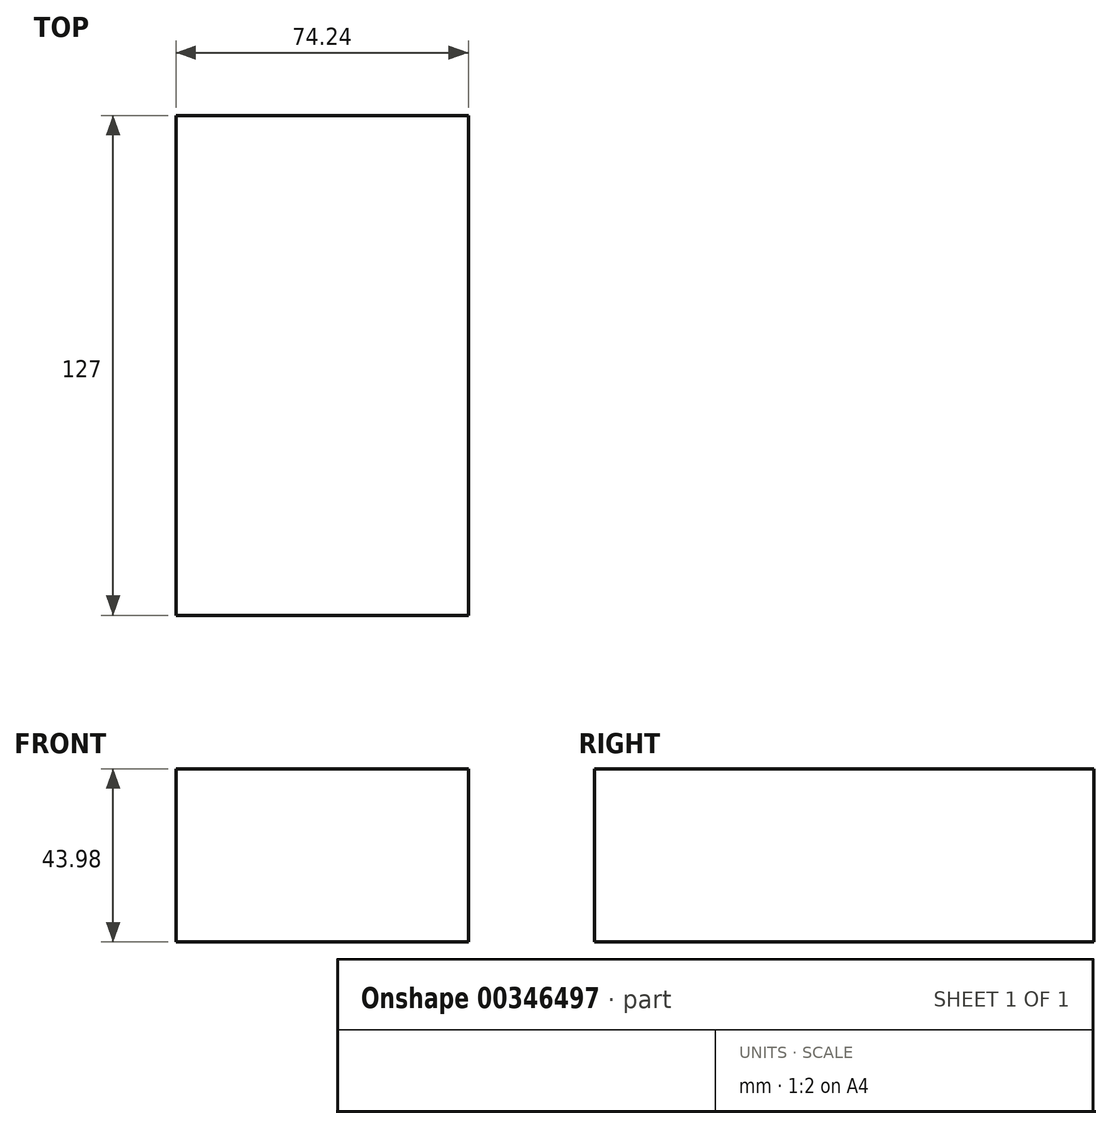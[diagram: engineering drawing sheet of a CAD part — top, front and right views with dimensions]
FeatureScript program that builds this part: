
annotation { "Feature Type Name" : "Feature", "Feature Type Description" : "" }
export const myFeature = defineFeature(function(context is Context, id is Id, definition is map)
    precondition{}
    {
        {
            var Q0;
            Q0=qCreatedBy(makeId("Front.planeOp"),FACE);
            var sketch = newSketch(context, id + "F0", { "sketchPlane" : qUnion([Q0])});
            skLineSegment(sketch, "E0.bottom", {"start": v(-37.12, -22) * mm, "end": v(37.12, -22) * mm});
            skLineSegment(sketch, "E0.top", {"start": v(-37.12, 22) * mm, "end": v(37.12, 22) * mm});
            skLineSegment(sketch, "E0.left", {"start": v(-37.12, -22) * mm, "end": v(-37.12, 22) * mm});
            skLineSegment(sketch, "E0.right", {"start": v(37.12, -22) * mm, "end": v(37.12, 22) * mm});
            skPoint(sketch, "E0.middle", {"position": v(0, 0) * mm});
            skLineSegment(sketch, "E1.bottom", {"start": v(102.12, 71.74) * mm, "end": v(38.27, 71.74) * mm});
            skLineSegment(sketch, "E1.top", {"start": v(102.12, 105.55) * mm, "end": v(38.27, 105.55) * mm});
            skLineSegment(sketch, "E1.left", {"start": v(102.12, 71.74) * mm, "end": v(102.12, 105.55) * mm});
            skLineSegment(sketch, "E1.right", {"start": v(38.27, 71.74) * mm, "end": v(38.27, 105.55) * mm});
            skPoint(sketch, "E1.middle", {"position": v(70.2, 88.65) * mm});
            skLineSegment(sketch, "E2", {"start": v(0, 22) * mm, "end": v(0, 49.77) * mm});
            skPoint(sketch, "E2.endSnap0", {"position": v(0, 22) * mm});
            skArc(sketch, "E3", {"start": v(0, 49.77) * mm, "mid": v(9.78, 73.37) * mm, "end": v(33.38, 83.15) * mm});
            skLineSegment(sketch, "E4", {"start": v(33.38, 83.15) * mm, "end": v(81.08, 83.15) * mm});
            skLineSegment(sketch, "E5.0", {"start": v(33.38, 95.09) * mm, "end": v(81.08, 95.09) * mm});
            skArc(sketch, "E5.1", {"start": v(-11.94, 49.77) * mm, "mid": v(1.33, 81.81) * mm, "end": v(33.38, 95.09) * mm});
            skLineSegment(sketch, "E5.2", {"start": v(-11.94, 22) * mm, "end": v(-11.94, 49.77) * mm});
            skLineSegment(sketch, "E6", {"start": v(81.08, 105.55) * mm, "end": v(81.08, 71.74) * mm});
            skSolve(sketch);
        }
        {
            var Q0;
            Q0=makeQuery(id+"F0.imprint","IMPRINT",FACE,{"disambiguationData":[TD([[makeQuery(id+"F0.imprint","IMPRINT",EDGE,{"derivedFrom":sQuery(id+"F0.wireOp",EDGE,"E0.bottom")}),1.0]])]});
            extrude(context, id + "F1", {"entities" : qUnion([Q0]), "endBound" : BoundingType.SYMMETRIC, "depth" : 127 * mm});
        }
        {
            var Q0;
            {var subQ1=sQuery(id+"F0.wireOp",EDGE,"E2");Q0=makeQuery(id+"F0.imprint","IMPRINT",FACE,{"disambiguationData":[TD([[makeQuery(id+"F0.imprint","IMPRINT",EDGE,{"derivedFrom":subQ1}),1.0]])]});}
            var Q1;
            Q1=sQuery(id+"F0.wireOp",EDGE,"E5.1");
            var Q2;
            Q2=sQuery(id+"F0.wireOp",EDGE,"E5.2");
            var Q3;
            Q3=sQuery(id+"F0.wireOp",EDGE,"E5.0");
            extrude(context, id + "F2", {"entities" : qUnion([Q0]), "bodyType" : ToolBodyType.SURFACE, "operationType" : NewBodyOperationType.INTERSECT, "surfaceEntities" : qUnion([Q1, Q2, Q3]), "endBound" : BoundingType.SYMMETRIC, "depth" : 25.4 * mm});
        }
        {
            var Q0;
            Q0=sQuery(id+"F0.wireOp",EDGE,"E4");
            extrude(context, id + "F3", {"bodyType" : ToolBodyType.SURFACE, "surfaceEntities" : qUnion([Q0]), "depth" : 25.4 * mm});
        }
    });
